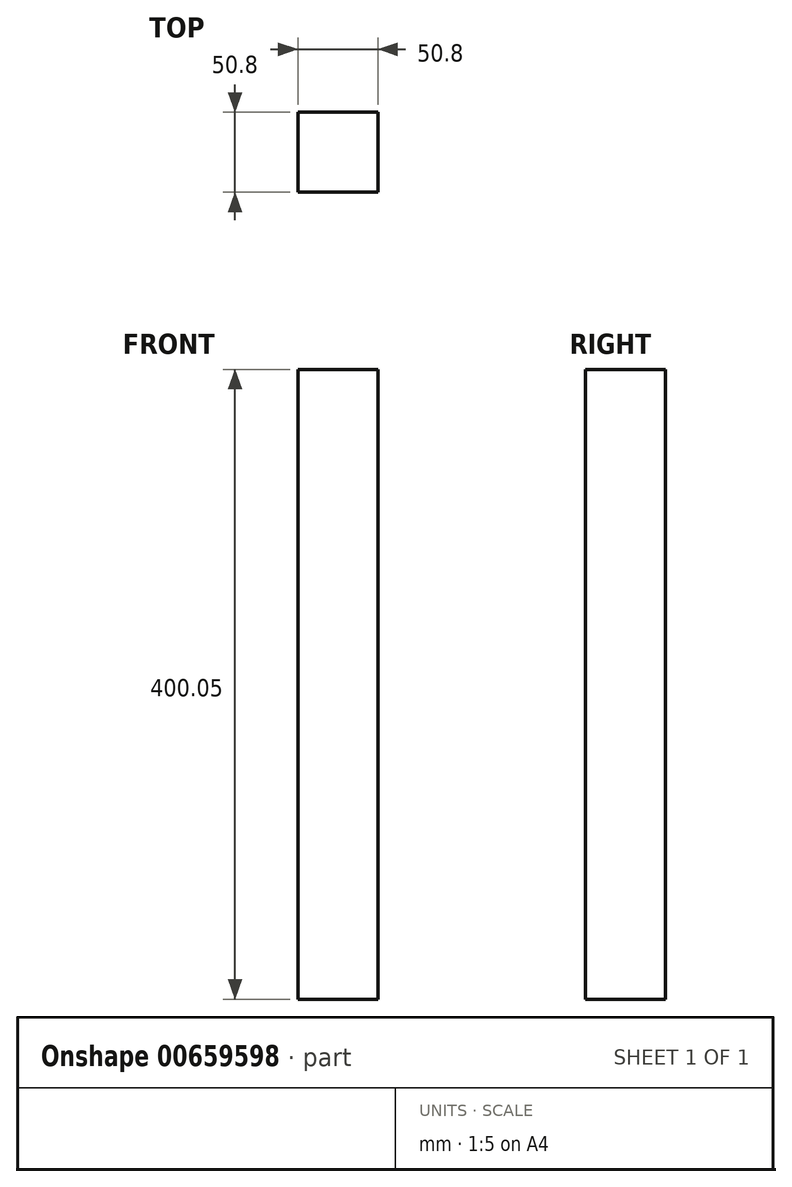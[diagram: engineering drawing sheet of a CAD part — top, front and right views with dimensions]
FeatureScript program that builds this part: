
annotation { "Feature Type Name" : "Feature", "Feature Type Description" : "" }
export const myFeature = defineFeature(function(context is Context, id is Id, definition is map)
    precondition{}
    {
        {
            var Q0;
            Q0=qCreatedBy(makeId("Top.planeOp"),FACE);
            var sketch = newSketch(context, id + "F0", { "sketchPlane" : qUnion([Q0])});
            skLineSegment(sketch, "E0.bottom", {"start": v(25.4, -25.4) * mm, "end": v(-25.4, -25.4) * mm});
            skLineSegment(sketch, "E0.top", {"start": v(25.4, 25.4) * mm, "end": v(-25.4, 25.4) * mm});
            skLineSegment(sketch, "E0.left", {"start": v(25.4, -25.4) * mm, "end": v(25.4, 25.4) * mm});
            skLineSegment(sketch, "E0.right", {"start": v(-25.4, -25.4) * mm, "end": v(-25.4, 25.4) * mm});
            skPoint(sketch, "E0.middle", {"position": v(0, 0) * mm});
            skSolve(sketch);
        }
        {
            var Q0;
            Q0 = qSketchRegion(id + "F0", true);
            var sketch = newSketch(context, id + "F1", { "sketchPlane" : qUnion([Q0])});
            skSolve(sketch);
        }
        {
            var Q0;
            Q0=makeQuery(id+"F1.imprint","IMPRINT",FACE,{"disambiguationData":[TD([[makeQuery(id+"F1.imprint","IMPRINT",EDGE,{"derivedFrom":makeQuery(id+"F0.imprint","IMPRINT",EDGE,{"derivedFrom":sQuery(id+"F0.wireOp",EDGE,"E0.bottom")})}),-1.0]])]});
            extrude(context, id + "F2", {"entities" : qUnion([Q0]), "depth" : 400.05 * mm, "offsetDistance" : 25 * mm});
        }
    });
